# Revit family: Metal_Lockers-Salsbury_Industries-18_51000_Series-1_Wide_Units
name_source: partatom
category: Specialty Equipment
units: mm (PartAtom-declared; Revit-internal decimal feet)

## family parameters
Always vertical = Yes
Cut with Voids When Loaded = No
Enable Cutting in Views = No
Maintain Annotation Orientation = No
OmniClass Number = 23.40.00.00
OmniClass Title = Equipment and Furnishings
Part Type = Normal
Room Calculation Point = No
Round Connector Dimension = Use Diameter
Shared = No
Work Plane-Based = No

## types (6) — shared parameters
Assembly Code = C1030310
Building Codes = https://www.lockers.com
Construction Details = https://www.lockers.com
Door Location D1 = Metal Locker Doors-18 inch with Hasps : Single Tier Door - 6 foot
Green Building-LEED = https://www.arcat.com
Hasp Handle Material = Plastic - Salsbury Finish - Black
Hasp Plate Rivet Material = Steel -Salsbury Finish - Polished Steel
Installation-Fabrication = https://www.lockers.com
Keynote = 10 51 00
Manufacturer = Salsbury Industries
Manufacturer Fax = 1-800-562-5399
Manufacturer Website = https://www.lockers.com
MasterFormat Number = 10 51 13
MasterFormat Title = Lockers
OmniClass 23 Number = 23.40.00.00
OmniClass 23 Title = Equipment and Furnishings
Product Data = https://www.lockers.com
Revision = R1_2018-10
Sales Information = https://www.lockers.com
Specification = https://www.lockers.com
Test Data = https://www.lockers.com
Type Comments = 18" Wide Standard Metal Locker - Single Tier
URL = www.lockers.com
Unit Height = 72 "
Version = 2.0 (02/28/18)
Width = 18.04 "
zero-valued in all types: Default Elevation

## per-type parameters (varying)
| type | Base Height | Depth | Description | Model | Sloping Corner Filler Offset | Sloping Hood Height | Standard Leg Base | Zee Base |
| 18-51161 - with Standard 6" High Legs | 6 " | 21.01 " | 1 Wide - 6 Feet High - 21 Inches Deep | 18-51161 | 77.68 " | 12.796 " | Metal Locker Legs : 6" High - 18"W x 21"D | Metal Locker Zee Base : None |
| 18-51168 - with Standard 6" High Legs | 6 " | 18.01 " | 1 Wide - 6 Feet High - 18 Inches Deep | 18-51168 | 77.68 " | 10.739 " | Metal Locker Legs : 6" High - 18"W x 18"D | Metal Locker Zee Base : None |
| 18-51161 - with 77575 Zee Base and 77550 Lockers without Legs | 4 " | 21.01 " | 1 Wide - 6 Feet High - 21 Inches Deep with Zee Base and Lockers without Legs | 18-51161 with 77575 and 77550 | 75.68 " | 12.796 " | Metal Locker Legs : No Legs | Metal Locker Zee Base : 77571 - 18"W x 21"D |
| 18-51168 - with 77578 Zee Base and 77550 Lockers without Legs | 4 " | 18.01 " | 1 Wide - 6 Feet High - 18 Inches Deep with Zee Base and Lockers without Legs | 18-51168 with 77578 and 77550 | 75.68 " | 10.739 " | Metal Locker Legs : No Legs | Metal Locker Zee Base : 77578 - 18"W x 18"D |
| 18-51161 - with 77550 Lockers without Legs | 0 " | 21.01 " | 1 Wide - 6 Feet High - 21 Inches Deep with Lockers without Legs | 18-51161 with 77550 | 71.68 " | 12.796 " | Metal Locker Legs : No Legs | Metal Locker Zee Base : None |
| 18-51168 - with 77550 Lockers without Legs | 0 " | 18.01 " | 1 Wide - 6 Feet High - 18 Inches Deep with Lockers without Legs | 18-51168 with 77550 | 71.68 " | 10.739 " | Metal Locker Legs : No Legs | Metal Locker Zee Base : None |

## geometry (parser evidence)
native form markers: Sweep x41
no freeform markers — native parametric forms only
